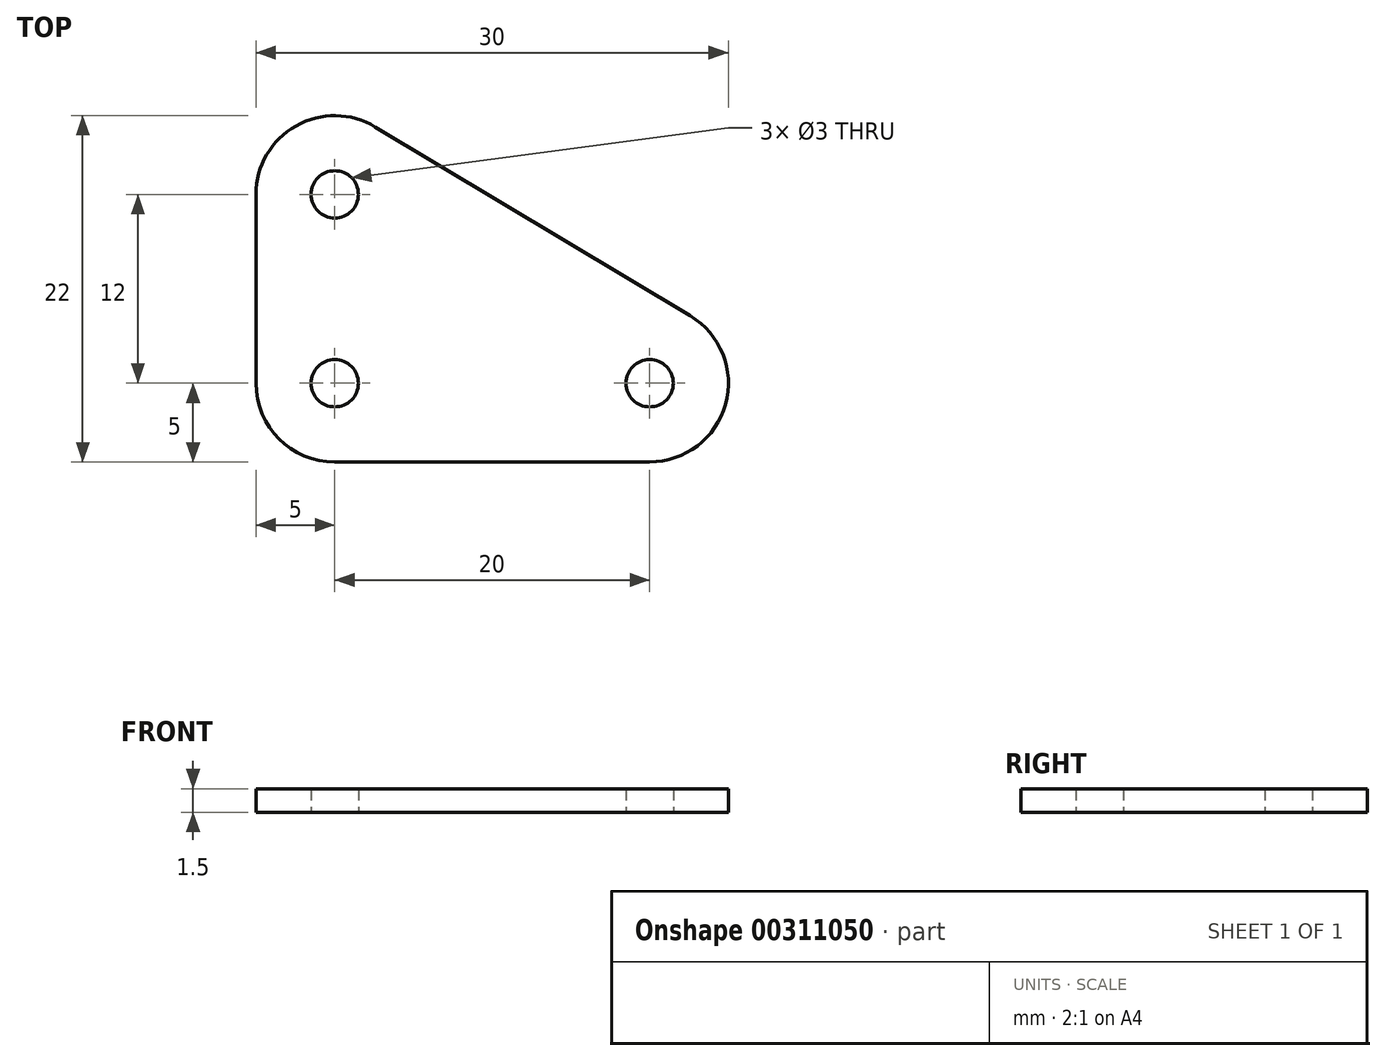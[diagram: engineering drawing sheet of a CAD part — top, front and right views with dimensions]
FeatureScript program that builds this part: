
annotation { "Feature Type Name" : "Feature", "Feature Type Description" : "" }
export const myFeature = defineFeature(function(context is Context, id is Id, definition is map)
    precondition{}
    {
        {
            var Q0;
            Q0=qCreatedBy(makeId("Top.planeOp"),FACE);
            var sketch = newSketch(context, id + "F0", { "sketchPlane" : qUnion([Q0])});
            skLineSegment(sketch, "E0", {"start": v(0, 5) * mm, "end": v(0, 17) * mm});
            skLineSegment(sketch, "E1", {"start": v(5, 0) * mm, "end": v(25, 0) * mm});
            skLineSegment(sketch, "E2", {"start": v(7.57, 21.29) * mm, "end": v(27.57, 9.29) * mm});
            skPoint(sketch, "E3.visualSharp", {"position": v(0, 25.83) * mm});
            skArc(sketch, "E3.filletArc", {"start": v(7.57, 21.29) * mm, "mid": v(2.54, 21.35) * mm, "end": v(0, 17) * mm});
            skPoint(sketch, "E4.visualSharp", {"position": v(43.05, 0) * mm});
            skArc(sketch, "E4.filletArc", {"start": v(25, 0) * mm, "mid": v(29.82, 3.67) * mm, "end": v(27.57, 9.29) * mm});
            skPoint(sketch, "E5.visualSharp", {"position": v(0, 0) * mm});
            skArc(sketch, "E5.filletArc", {"start": v(0, 5) * mm, "mid": v(1.46, 1.46) * mm, "end": v(5, 0) * mm});
            skCircle(sketch, "E6", {"center": v(5, 5) * mm, "radius": 1.5 * mm});
            skCircle(sketch, "E7", {"center": v(25, 5) * mm, "radius": 1.5 * mm});
            skCircle(sketch, "E8", {"center": v(5, 17) * mm, "radius": 1.5 * mm});
            skSolve(sketch);
        }
        {
            var Q0;
            Q0=makeQuery(id+"F0.imprint","IMPRINT",FACE,{"disambiguationData":[TD([[makeQuery(id+"F0.imprint","IMPRINT",EDGE,{"derivedFrom":sQuery(id+"F0.wireOp",EDGE,"E0")}),-1.0]])]});
            extrude(context, id + "F1", {"entities" : qUnion([Q0]), "depth" : 1.5 * mm});
        }
    });
